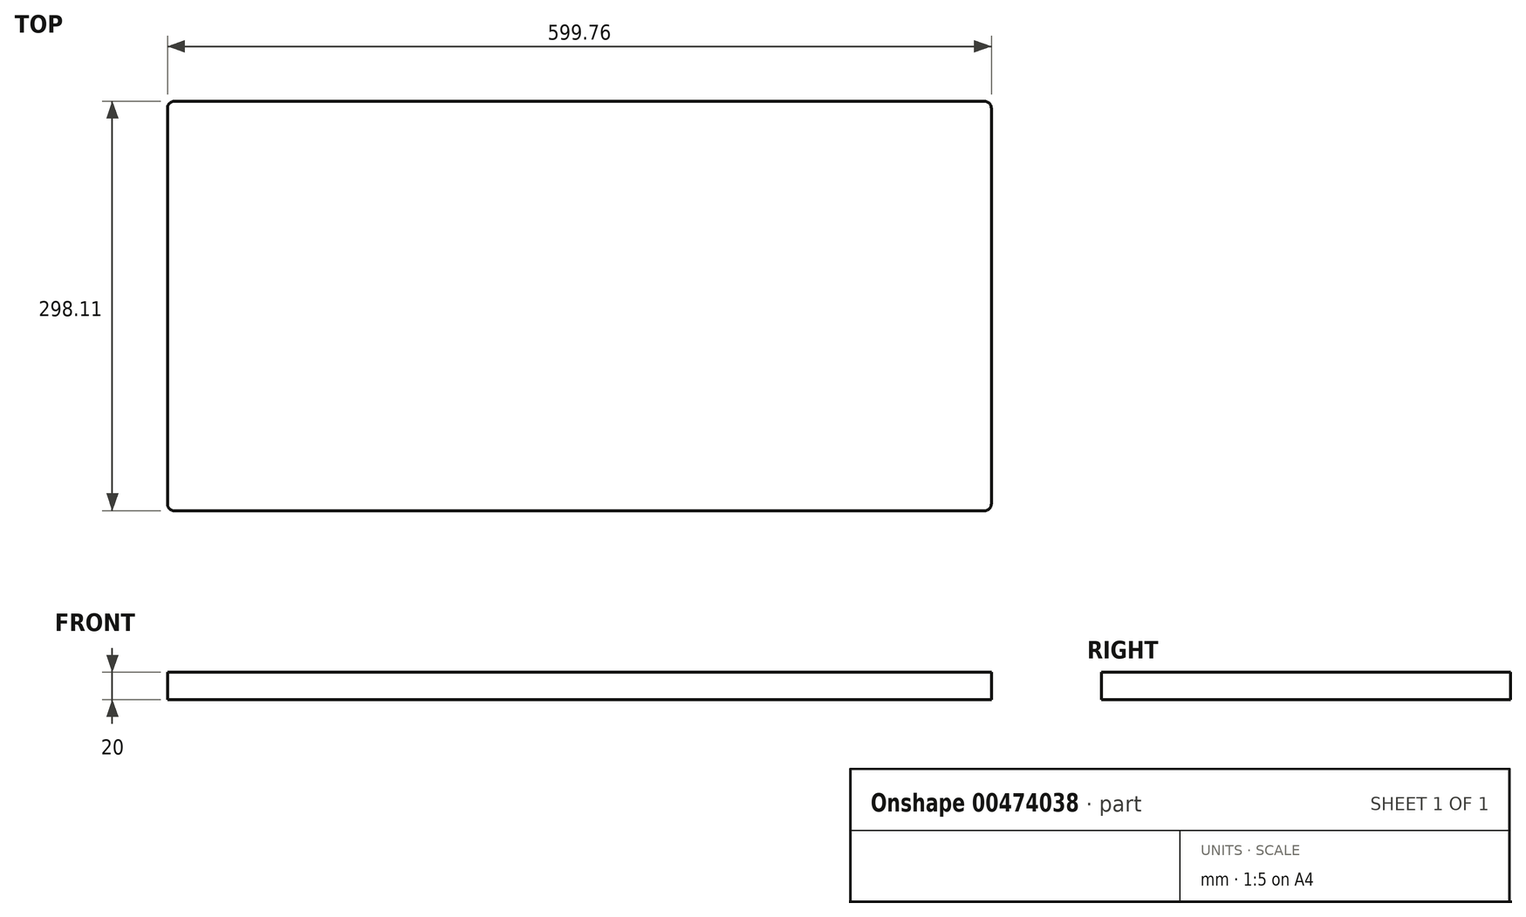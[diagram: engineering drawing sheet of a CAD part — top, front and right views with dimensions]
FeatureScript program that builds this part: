
annotation { "Feature Type Name" : "Feature", "Feature Type Description" : "" }
export const myFeature = defineFeature(function(context is Context, id is Id, definition is map)
    precondition{}
    {
        {
            var Q0;
            Q0=qCreatedBy(makeId("Top.planeOp"),FACE);
            var sketch = newSketch(context, id + "F0", { "sketchPlane" : qUnion([Q0])});
            skLineSegment(sketch, "E0.bottom", {"start": v(0, 153.36) * mm, "end": v(-294.88, 153.36) * mm});
            skLineSegment(sketch, "E0.top", {"start": v(0, -144.75) * mm, "end": v(-294.88, -144.75) * mm});
            skLineSegment(sketch, "E0.left", {"start": v(0, 153.36) * mm, "end": v(0, -144.75) * mm});
            skLineSegment(sketch, "E0.right", {"start": v(-299.88, 148.36) * mm, "end": v(-299.88, -139.75) * mm});
            skPoint(sketch, "E1.visualSharp", {"position": v(-299.88, 153.36) * mm});
            skArc(sketch, "E1.filletArc", {"start": v(-294.88, 153.36) * mm, "mid": v(-298.42, 151.9) * mm, "end": v(-299.88, 148.36) * mm});
            skPoint(sketch, "E2.visualSharp", {"position": v(-299.88, -144.75) * mm});
            skArc(sketch, "E2.filletArc", {"start": v(-299.88, -139.75) * mm, "mid": v(-298.42, -143.29) * mm, "end": v(-294.88, -144.75) * mm});
            skSolve(sketch);
        }
        {
            var Q0;
            Q0 = qSketchRegion(id + "F0", true);
            extrude(context, id + "F1", {"entities" : qUnion([Q0]), "depth" : 20 * mm});
        }
        {
            var Q0;
            Q0=makeQuery(id+"F1.opExtrude","SWEPT_BODY",BODY,{"disambiguationData":[OSD([sQuery(id+"F0.wireOp",EDGE,"E0.bottom"),sQuery(id+"F0.wireOp",EDGE,"E0.top"),sQuery(id+"F0.wireOp",EDGE,"E0.left"),sQuery(id+"F0.wireOp",EDGE,"E0.right"),sQuery(id+"F0.wireOp",EDGE,"E1.filletArc"),sQuery(id+"F0.wireOp",EDGE,"E2.filletArc")])]});
            var Q1;
            Q1=makeQuery(id+"F1.opExtrude","SWEPT_FACE",FACE,{"disambiguationData":[OSD([sQuery(id+"F0.wireOp",EDGE,"E0.left")])]});
            mirror(context, id + "F2", {"operationType" : NewBodyOperationType.ADD, "entities" : qUnion([Q0]), "mirrorPlane" : qUnion([Q1])});
        }
    });
